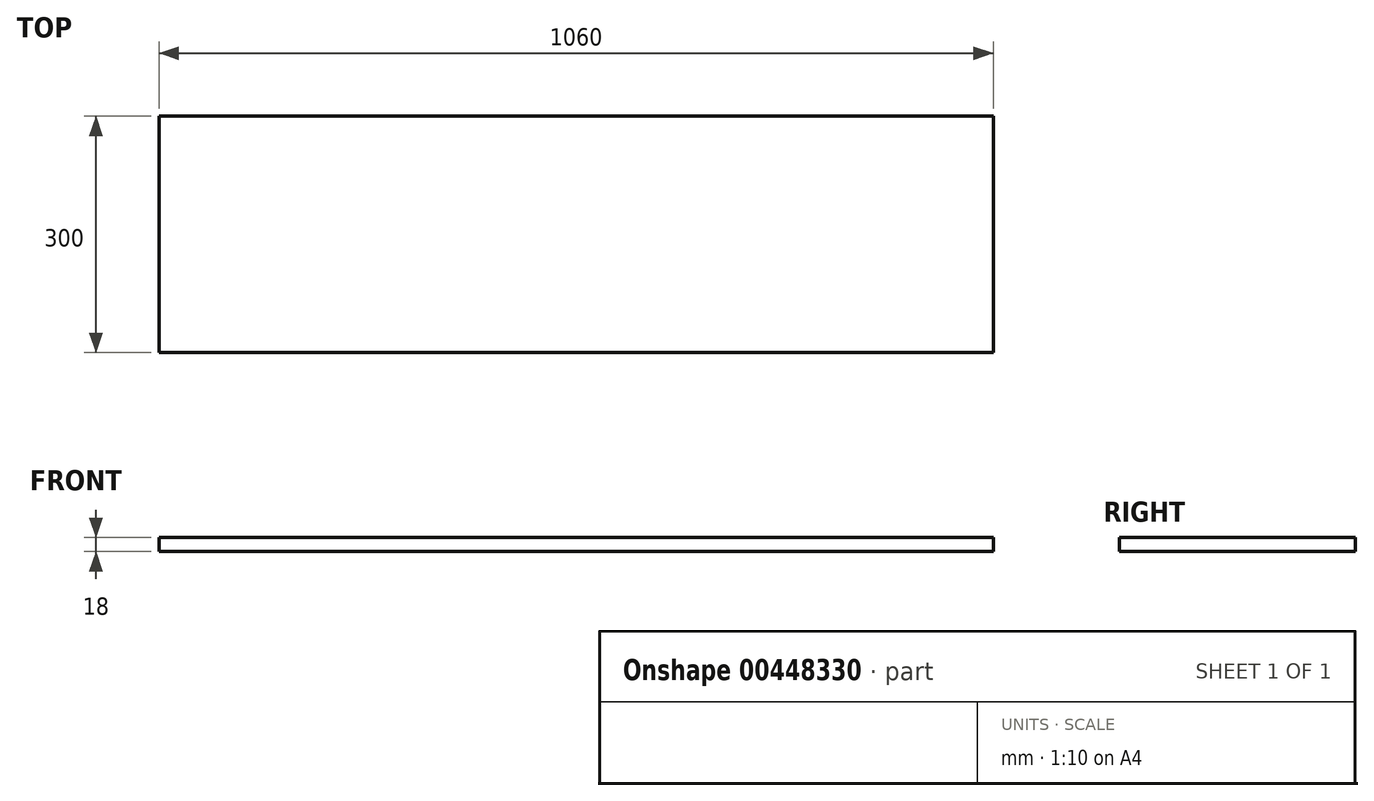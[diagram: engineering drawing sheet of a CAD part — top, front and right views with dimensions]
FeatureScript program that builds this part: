
annotation { "Feature Type Name" : "Feature", "Feature Type Description" : "" }
export const myFeature = defineFeature(function(context is Context, id is Id, definition is map)
    precondition{}
    {
        {
            var Q0;
            Q0=qCreatedBy(makeId("Top.planeOp"),FACE);
            var sketch = newSketch(context, id + "F0", { "sketchPlane" : qUnion([Q0])});
            skLineSegment(sketch, "E0.bottom", {"start": v(0, 0) * mm, "end": v(1060, 0) * mm});
            skLineSegment(sketch, "E0.top", {"start": v(0, 300) * mm, "end": v(1060, 300) * mm});
            skLineSegment(sketch, "E0.left", {"start": v(0, 0) * mm, "end": v(0, 300) * mm});
            skLineSegment(sketch, "E0.right", {"start": v(1060, 0) * mm, "end": v(1060, 300) * mm});
            skSolve(sketch);
        }
        {
            var Q0;
            Q0=makeQuery(id+"F0.imprint","IMPRINT",FACE,{"disambiguationData":[TD([[makeQuery(id+"F0.imprint","IMPRINT",EDGE,{"derivedFrom":sQuery(id+"F0.wireOp",EDGE,"E0.bottom")}),1.0]])]});
            extrude(context, id + "F1", {"entities" : qUnion([Q0]), "depth" : 18 * mm});
        }
    });
